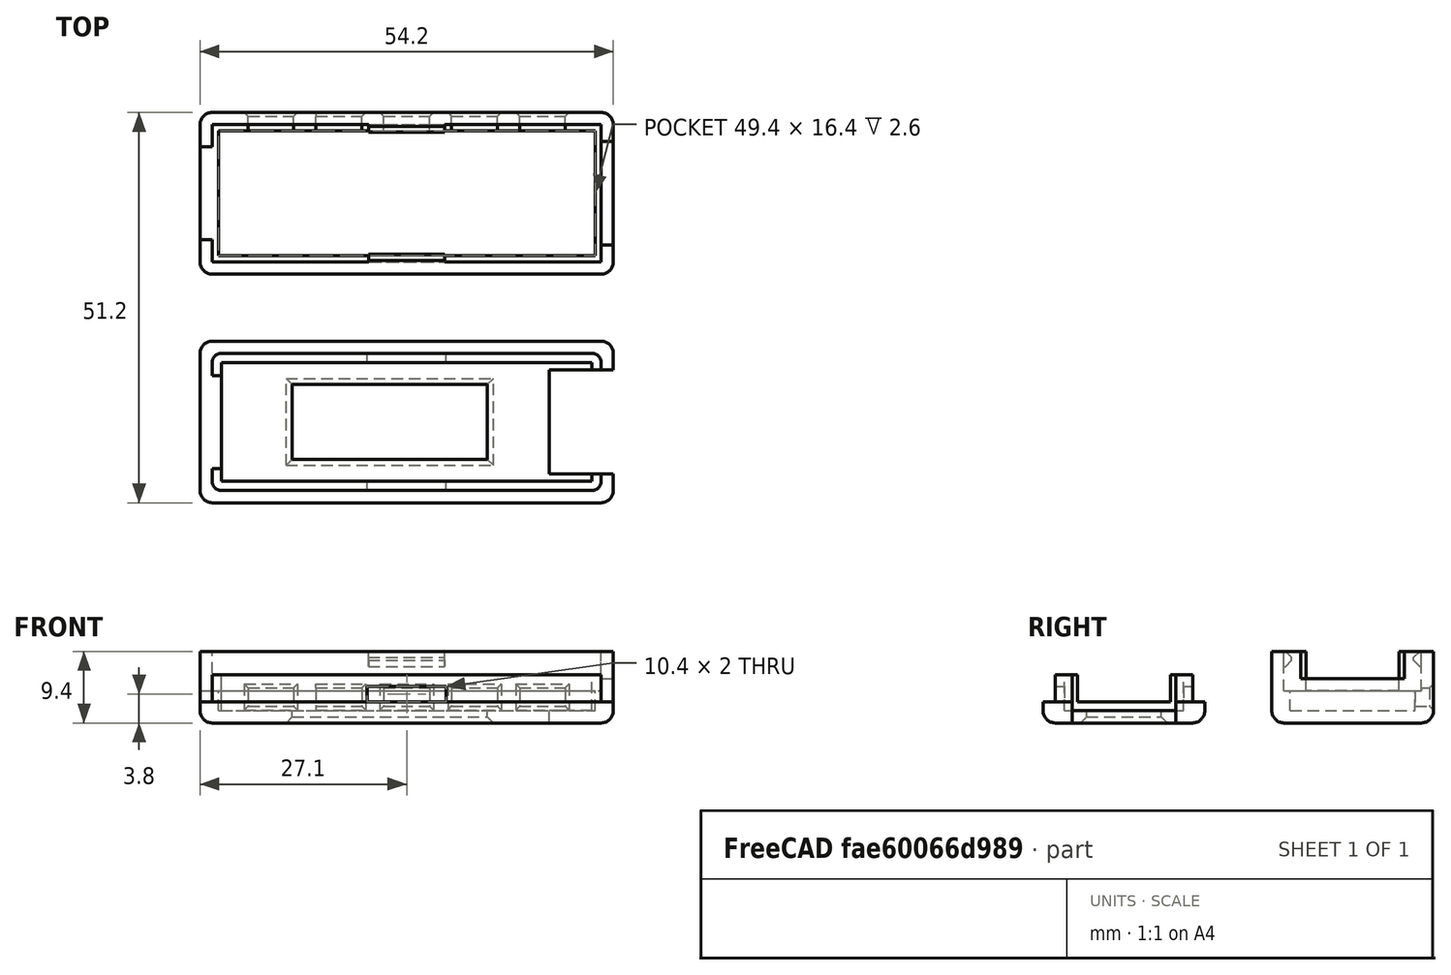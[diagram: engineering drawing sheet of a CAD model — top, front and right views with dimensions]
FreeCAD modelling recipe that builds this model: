
FCSTD DOCUMENT  (FreeCAD 0.16R)
Label: PhoneChargeGuard_v0.2
License: All rights reserved
LicenseURL: http://en.wikipedia.org/wiki/All_rights_reserved
objects: Part::Box×22, Part::Cut×6, Part::Chamfer×4, Part::MultiFuse×4, Part::Fillet×3
note: 39 computed .brp shape members not serialized (recipe doc carries the construction recipe); baked Part::Feature solids carry a one-line shape summary decoded from their .brp

FEATURE [Part::Box] Box  label="unten_außen"
  Height = 9.4
  Length = 54.2
  Placement = pos=(-1.6,-1.6,0) rot=(0,0,1;0rad)
  Width = 21.2
FEATURE [Part::Box] Box001  label="unten_innen"
  Height = 9.4
  Length = 51
  Placement = pos=(0,0,1.6) rot=(0,0,1;0rad)
  Width = 18
FEATURE [Part::Cut] Cut  label="Schale_roh"
  Base = -> Box
  Tool = -> Box001
FEATURE [Part::Fillet] Fillet  label="Schale_unten"
  Base = -> Cut
  Edges = 8 edges r=1.6: [Edge1,Edge3,Edge4,Edge5,Edge6,Edge14,Edge15,Edge16]
FEATURE [Part::Box] Box002  label="Auflage_außen"
  Height = 2.6
  Length = 51
  Placement = pos=(0,0,1.6) rot=(0,0,1;0rad)
  Width = 18
FEATURE [Part::Box] Box003  label="Auflage_innen"
  Height = 2.6
  Length = 49.4
  Placement = pos=(0.8,0.8,1.6) rot=(0,0,1;0rad)
  Width = 16.4
FEATURE [Part::Cut] Cut001  label="Auflage"
  Base = -> Box002
  Tool = -> Box003
FEATURE [Part::Box] Box004  label="Haken1_roh"
  Height = 2
  Length = 10
  Placement = pos=(20.5,0,7.4) rot=(0,0,1;0rad)
  Width = 1
FEATURE [Part::Chamfer] Chamfer  label="Haken1"
  Base = -> Box004
  Edges = 2 edges r=0.8: [Edge11,Edge12]
FEATURE [Part::Box] Box005  label="Haken2_roh"
  Height = 2
  Length = 10
  Placement = pos=(20.5,17,7.4) rot=(0,0,1;0rad)
  Width = 1
FEATURE [Part::Chamfer] Chamfer001  label="Haken2"
  Base = -> Box005
  Edges = 2 edges r=0.8: [Edge9,Edge10]
FEATURE [Part::Box] Box006  label="USB_Stecker"
  Height = 5.2
  Length = 10
  Placement = pos=(-5,2.9,4.2) rot=(0,0,1;0rad)
  Width = 12.2
FEATURE [Part::Box] Box007  label="USB_Buchse"
  Height = 10
  Length = 10
  Placement = pos=(48,2.2,5.8) rot=(0,0,1;0rad)
  Width = 13.6
FEATURE [Part::Box] Box008  label="Button1"
  Height = 2.4
  Length = 6
  Placement = pos=(4.7,14,2.2) rot=(0,0,1;0rad)
  Width = 10
FEATURE [Part::Box] Box009  label="Button2"
  Height = 2.4
  Length = 6
  Placement = pos=(13.6,14,2.2) rot=(0,0,1;0rad)
  Width = 10
FEATURE [Part::Box] Box010  label="oben_außen"
  Height = 2.8
  Length = 54.2
  Placement = pos=(-1.6,-31.6,0) rot=(0,0,1;0rad)
  Width = 21.2
FEATURE [Part::Box] Box011  label="oben_innen"
  Height = 9.4
  Length = 51
  Placement = pos=(0,-30,1.6) rot=(0,0,1;0rad)
  Width = 18
FEATURE [Part::Cut] Cut002  label="Schale_oben_roh"
  Base = -> Box010
  Tool = -> Box011
FEATURE [Part::Fillet] Fillet001  label="Schale_oben"
  Base = -> Cut002
  Edges = 8 edges r=1.6: [Edge1,Edge3,Edge4,Edge5,Edge6,Edge14,Edge15,Edge16]
FEATURE [Part::Box] Box012  label="Rahmen_außen"
  Height = 4.7
  Length = 51
  Placement = pos=(0,-30,1.6) rot=(0,0,1;0rad)
  Width = 18
FEATURE [Part::Box] Box013  label="Rahmen_innen"
  Height = 4.8
  Length = 48.6
  Placement = pos=(1.2,-28.8,1.6) rot=(0,0,1;0rad)
  Width = 15.6
FEATURE [Part::Cut] Cut003  label="Rahmen"
  Base = -> Box012
  Tool = -> Box013
FEATURE [Part::Box] Box014  label="OLED"
  Height = 1.6
  Length = 25.6
  Placement = pos=(10.5,-25.9,0) rot=(0,0,1;0rad)
  Width = 9.8
FEATURE [Part::Box] Box015  label="USB_Stecker2"
  Height = 5.2
  Length = 10
  Placement = pos=(-5,-27.1,2.8) rot=(0,0,1;0rad)
  Width = 12.2
FEATURE [Part::Box] Box016  label="USB_Buchse2"
  Height = 10
  Length = 10
  Placement = pos=(44.2,-27.8,0) rot=(0,0,1;0rad)
  Width = 13.6
FEATURE [Part::Box] Box017  label="Oese1"
  Height = 2
  Length = 10.4
  Placement = pos=(20.3,-33,2.8) rot=(0,0,1;0rad)
  Width = 5
FEATURE [Part::Box] Box018  label="Oese2"
  Height = 2
  Length = 10.4
  Placement = pos=(20.3,-15,2.8) rot=(0,0,1;0rad)
  Width = 5
FEATURE [Part::Box] Box019  label="Button3"
  Height = 2.4
  Length = 6
  Placement = pos=(22.5,14,2.2) rot=(0,0,1;0rad)
  Width = 10
FEATURE [Part::Box] Box020  label="Button4"
  Height = 2.4
  Length = 6
  Placement = pos=(31.4,14,2.2) rot=(0,0,1;0rad)
  Width = 10
FEATURE [Part::Box] Box021  label="Button5"
  Height = 2.4
  Length = 6
  Placement = pos=(40.3,14,2.2) rot=(0,0,1;0rad)
  Width = 10
FEATURE [Part::MultiFuse] Fusion  label="bottom_raw"
  Shapes = -> [Fillet,Cut001,Chamfer001,Chamfer]
FEATURE [Part::MultiFuse] Fusion001  label="bottom_cutouts"
  Shapes = -> [Box006,Box007,Box008,Box009,Box019,Box020,Box021]
FEATURE [Part::MultiFuse] Fusion002  label="top_raw"
  Shapes = -> [Fillet001,Cut003]
FEATURE [Part::MultiFuse] Fusion003  label="top_cutouts"
  Shapes = -> [Box014,Box015,Box016,Box017,Box018]
FEATURE [Part::Cut] Cut004  label="case_bottom_raw"
  Base = -> Fusion
  Tool = -> Fusion001
FEATURE [Part::Cut] Cut005  label="case_top_raw"
  Base = -> Fusion002
  Tool = -> Fusion003
FEATURE [Part::Chamfer] Chamfer002  label="case_bottom"
  Base = -> Cut004
  Edges = 19 edges r=0.5: [Edge75,Edge76,Edge77,Edge78,Edge79,Edge80,Edge81,Edge82,Edge83,Edge84,Edge85,Edge87,Edge88,Edge89,Edge90,Edge91,Edge92,Edge93,Edge94]
FEATURE [Part::Chamfer] Chamfer003  label="case_top_raw2"
  Base = -> Cut005
  Edges = 4 edges r=0.8: [Edge54,Edge55,Edge56,Edge57]
FEATURE [Part::Fillet] Fillet002  label="case_top"
  Base = -> Chamfer003
  Edges = 4 edges r=1.2: [Edge82,Edge102,Edge129,Edge149]
